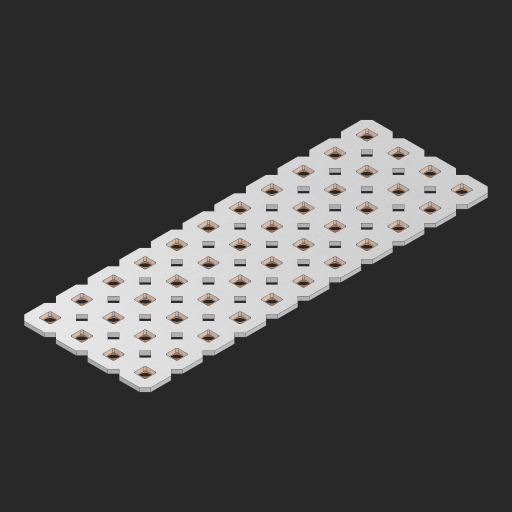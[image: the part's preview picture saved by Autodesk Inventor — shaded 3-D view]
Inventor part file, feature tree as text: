
AUTODESK INVENTOR PART (.ipt)
format: ipt  version: 2023 (Build 270158000, 158)  size: 799,232 bytes
history: native  units: in
note: dims shown in document units (in); Inventor stores cm internally (conversion verified against a paired STEP export)
features: other x45, extrude x43, sketch x2, pattern_linear x1
ambient origin geometry x8: Origin, YZ Plane, XZ Plane, XY Plane, X Axis, Y Axis, Z Axis, Center Point
bodies: Solid1 (feature_tree), Body (feature_tree)
feature tree (91):
  pattern_linear  "Rectangular Pattern1"  Spacing1=0.09in  [1 undecoded]
  sketch  "Sketch1"  dims[d1=0.5in]
  sketch  "Sketch2"  dims[d2=0.182in d3=0.09in d4=0.09in d5=0.09in d6=0.09in d7=0.09in d8=0.09in d9=0.09in d10=0.09in d11=0.02in d13=0.0in d14=0.172in d15=0.0625in d16=0.0in d19=0.5in d22=0.5in]
  other  "Srf1"
  other  "Srf126"
  other  "Srf127"
  other  "Srf128"
  other  "Srf129"
  other  "Srf130"
  other  "Srf131"
  other  "Srf250"
  other  "Srf251"
  other  "Srf252"
  other  "Srf253"
  other  "Srf268"
  other  "Srf269"
  other  "Srf270"
  other  "Srf271"
  other  "Srf272"
  other  "Srf273"
  other  "Srf274"
  other  "Srf275"
  other  "Srf276"
  other  "Srf277"
  other  "Srf278"
  other  "Srf293"
  other  "Srf294"
  other  "Srf295"
  other  "Srf296"
  other  "Srf297"
  other  "Srf298"
  other  "Srf299"
  other  "Srf300"
  other  "Srf301"
  other  "Srf302"
  other  "Srf303"
  other  "Srf318"
  other  "Srf319"
  other  "Srf320"
  other  "Srf321"
  other  "Srf322"
  other  "Srf323"
  other  "Srf324"
  other  "Srf325"
  other  "Srf326"
  other  "Srf327"
  other  "Srf328"
  other  "Circle"
  extrude  "ExtrusionSrf126"  Depth=0.09in
  extrude  "ExtrusionSrf127"  Depth=0.09in
  extrude  "ExtrusionSrf128"  Depth=0.09in
  extrude  "ExtrusionSrf129"  Depth=0.09in
  extrude  "ExtrusionSrf130"  Depth=0.09in
  extrude  "ExtrusionSrf131"  Depth=0.09in
  extrude  "ExtrusionSrf250"  Depth=0.09in
  extrude  "ExtrusionSrf251"  Depth=0.02in
  extrude  "ExtrusionSrf252"  TaperAngle=0.0deg  [1 undecoded]
  extrude  "ExtrusionSrf253"  Depth=0.5in
  extrude  "ExtrusionSrf268"  Depth=0.0625in TaperAngle=0.0deg
  extrude  "ExtrusionSrf269"  Depth=0.5in
  extrude  "ExtrusionSrf270"  Depth=0.5in
  extrude  "ExtrusionSrf271"  [1 undecoded]
  extrude  "ExtrusionSrf272"  [1 undecoded]
  extrude  "ExtrusionSrf273"  [1 undecoded]
  extrude  "ExtrusionSrf274"  [1 undecoded]
  extrude  "ExtrusionSrf275"  [1 undecoded]
  extrude  "ExtrusionSrf276"  [1 undecoded]
  extrude  "ExtrusionSrf277"  [1 undecoded]
  extrude  "ExtrusionSrf278"  [1 undecoded]
  extrude  "ExtrusionSrf293"  [1 undecoded]
  extrude  "ExtrusionSrf294"  [1 undecoded]
  extrude  "ExtrusionSrf295"  [1 undecoded]
  extrude  "ExtrusionSrf296"  [1 undecoded]
  extrude  "ExtrusionSrf297"  [1 undecoded]
  extrude  "ExtrusionSrf298"  [1 undecoded]
  extrude  "ExtrusionSrf299"  [1 undecoded]
  extrude  "ExtrusionSrf300"  [1 undecoded]
  extrude  "ExtrusionSrf301"  [1 undecoded]
  extrude  "ExtrusionSrf302"  [1 undecoded]
  extrude  "ExtrusionSrf303"  [1 undecoded]
  extrude  "ExtrusionSrf318"  [1 undecoded]
  extrude  "ExtrusionSrf319"  [1 undecoded]
  extrude  "ExtrusionSrf320"  [1 undecoded]
  extrude  "ExtrusionSrf321"  [1 undecoded]
  extrude  "ExtrusionSrf322"  [1 undecoded]
  extrude  "ExtrusionSrf323"  [1 undecoded]
  extrude  "ExtrusionSrf324"  [1 undecoded]
  extrude  "ExtrusionSrf325"  [1 undecoded]
  extrude  "ExtrusionSrf326"  [1 undecoded]
  extrude  "ExtrusionSrf327"  [1 undecoded]
  extrude  "ExtrusionSrf328"  [1 undecoded]
note: 32 required parameter values undecoded (feature->parameter linkage not recoverable at this tier; creation-order binding heuristic only, values carry confidence <= 0.55)
